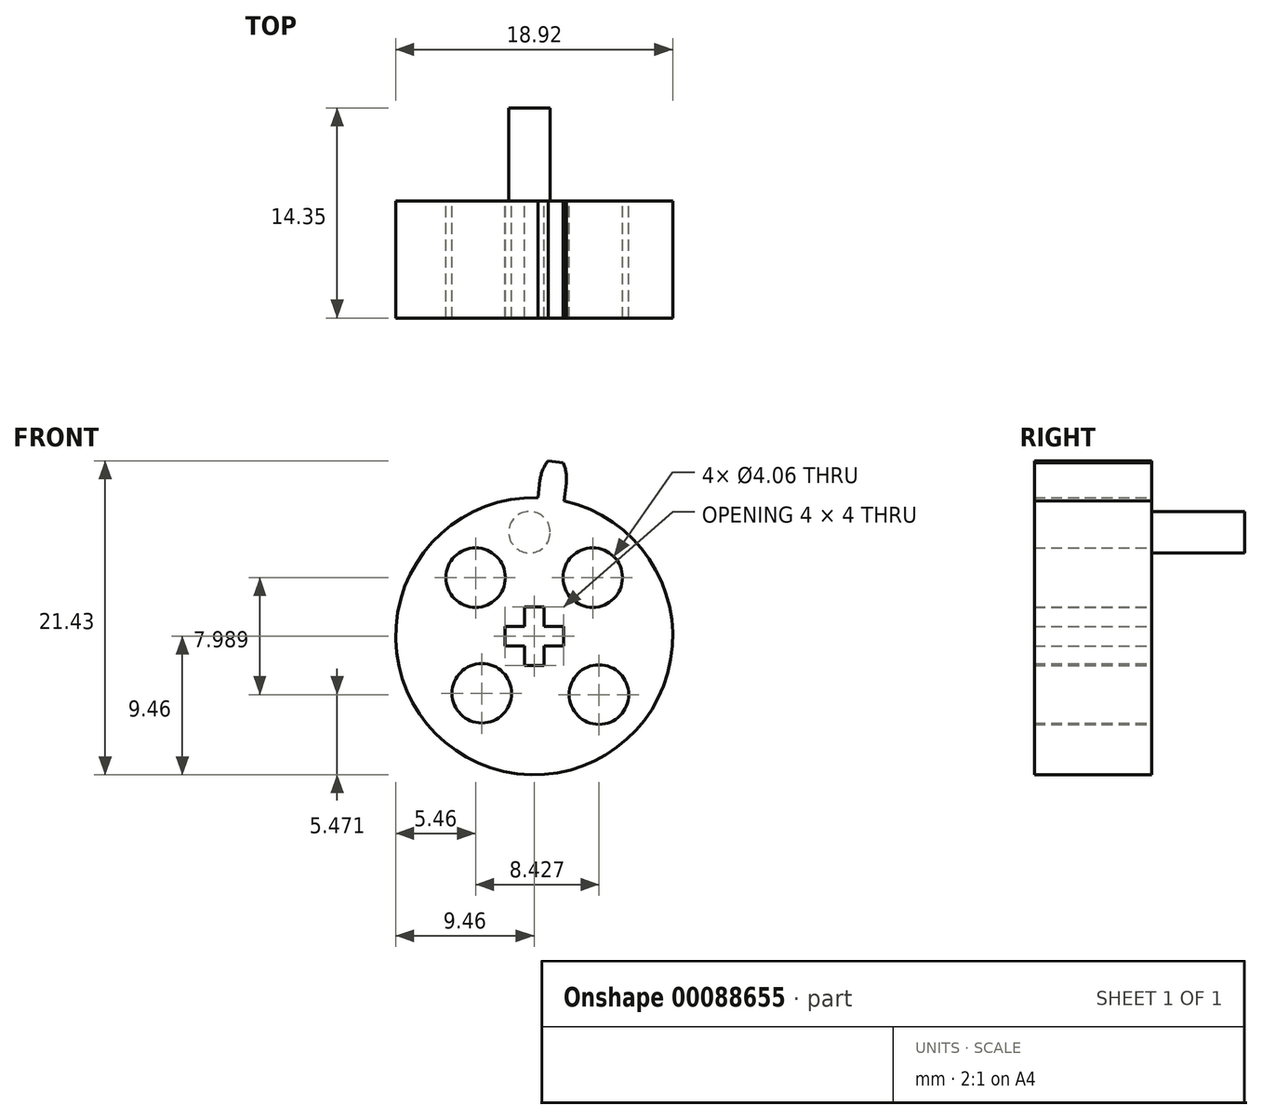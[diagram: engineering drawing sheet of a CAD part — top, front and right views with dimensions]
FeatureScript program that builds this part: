
annotation { "Feature Type Name" : "Feature", "Feature Type Description" : "" }
export const myFeature = defineFeature(function(context is Context, id is Id, definition is map)
    precondition{}
    {
        {
            var Q0;
            Q0=qCreatedBy(makeId("Front.planeOp"),FACE);
            var sketch = newSketch(context, id + "F0", { "sketchPlane" : qUnion([Q0])});
            skLineSegment(sketch, "E0", {"start": v(0.96, 11.97) * mm, "end": v(1.97, 11.85) * mm});
            skArc(sketch, "E1", {"start": v(0.25, 9.46) * mm, "mid": v(1.15, 9.39) * mm, "end": v(2.05, 9.24) * mm});
            skLineSegment(sketch, "E2", {"start": v(0.4, 10.67) * mm, "end": v(0.25, 9.46) * mm});
            skLineSegment(sketch, "E3.MirrorCS", {"start": v(2.2, 10.45) * mm, "end": v(2.05, 9.24) * mm});
            skLineSegment(sketch, "E4", {"start": v(1.15, 9.39) * mm, "end": v(1.5, 12.2) * mm, "construction": true});
            skArc(sketch, "E5", {"start": v(0.96, 11.97) * mm, "mid": v(0.59, 11.36) * mm, "end": v(0.4, 10.67) * mm});
            skArc(sketch, "E6", {"start": v(2.2, 10.45) * mm, "mid": v(2.18, 11.16) * mm, "end": v(1.97, 11.85) * mm});
            skSolve(sketch);
        }
        {
            var Q0;
            Q0=qCreatedBy(makeId("Top.planeOp"),FACE);
            var sketch = newSketch(context, id + "F1", { "sketchPlane" : qUnion([Q0])});
            skLineSegment(sketch, "E7", {"start": v(0, 0) * mm, "end": v(0, 30.53) * mm, "construction": true});
            skLineSegment(sketch, "E8", {"start": v(0, 0) * mm, "end": v(0, -25.91) * mm, "construction": true});
            skSolve(sketch);
        }
        {
            var Q0;
            Q0=qCreatedBy(makeId("Front.planeOp"),FACE);
            var sketch = newSketch(context, id + "F2", { "sketchPlane" : qUnion([Q0])});
            skCircle(sketch, "E9", {"center": v(0, 0) * mm, "radius": 9.46 * mm});
            skCircle(sketch, "E10", {"center": v(-4, 4) * mm, "radius": 2.03 * mm});
            skCircle(sketch, "E11.1.0.0", {"center": v(4, 4) * mm, "radius": 2.03 * mm});
            skLineSegment(sketch, "E11.direction1", {"start": v(-4, 4) * mm, "end": v(4, 4) * mm, "construction": true});
            skCircle(sketch, "E12.0.1.0", {"center": v(4.43, -3.99) * mm, "radius": 2.03 * mm});
            skLineSegment(sketch, "E12.direction1", {"start": v(4, 4) * mm, "end": v(23.14, 4) * mm, "construction": true});
            skLineSegment(sketch, "E12.direction2", {"start": v(4, 4) * mm, "end": v(4.43, -3.99) * mm, "construction": true});
            skCircle(sketch, "E13.1.0.0", {"center": v(-3.57, -3.9) * mm, "radius": 2.03 * mm});
            skLineSegment(sketch, "E13.direction1", {"start": v(4.43, -3.99) * mm, "end": v(-3.57, -3.9) * mm, "construction": true});
            skSolve(sketch);
        }
        {
            var Q0;
            Q0=makeQuery(id+"F2.imprint","IMPRINT",FACE,{"disambiguationData":[TD([[makeQuery(id+"F2.imprint","IMPRINT",EDGE,{"derivedFrom":sQuery(id+"F2.wireOp",EDGE,"E9")}),1.0]])]});
            extrude(context, id + "F3", {"entities" : qUnion([Q0]), "depth" : 8 * mm});
        }
        {
            var Q0;
            Q0=makeQuery(id+"F0.imprint","IMPRINT",FACE,{"disambiguationData":[TD([[makeQuery(id+"F0.imprint","IMPRINT",EDGE,{"derivedFrom":sQuery(id+"F0.wireOp",EDGE,"E0")}),-1.0]])]});
            var Q1;
            Q1=makeQuery(id+"F3.opExtrude","CAP_FACE",FACE,{"disambiguationData":[OSD([sQuery(id+"F2.wireOp",EDGE,"E9"),sQuery(id+"F2.wireOp",EDGE,"E10"),sQuery(id+"F2.wireOp",EDGE,"E11.1.0.0"),sQuery(id+"F2.wireOp",EDGE,"E12.0.1.0"),sQuery(id+"F2.wireOp",EDGE,"E13.1.0.0")])],"isStart":false});
            extrude(context, id + "F4", {"entities" : qUnion([Q0]), "operationType" : NewBodyOperationType.ADD, "endBound" : BoundingType.UP_TO_SURFACE, "endBoundEntityFace" : qUnion([Q1]), "depth" : 25.4 * mm});
        }
        {
            var Q0;
            Q0=qCreatedBy(makeId("Front.planeOp"),FACE);
            var sketch = newSketch(context, id + "F5", { "sketchPlane" : qUnion([Q0])});
            skLineSegment(sketch, "E14", {"start": v(0, 3.5) * mm, "end": v(0, -4.5) * mm, "construction": true});
            skLineSegment(sketch, "E15", {"start": v(0.67, 2) * mm, "end": v(0.67, 0.67) * mm});
            skLineSegment(sketch, "E16", {"start": v(0.67, 0.67) * mm, "end": v(2, 0.67) * mm});
            skLineSegment(sketch, "E17", {"start": v(2, 0.67) * mm, "end": v(2, 0) * mm});
            skLineSegment(sketch, "E18", {"start": v(0.67, 2) * mm, "end": v(0, 2) * mm});
            skLineSegment(sketch, "E19", {"start": v(3.85, 0) * mm, "end": v(-2.03, 0) * mm, "construction": true});
            skArc(sketch, "E20.0", {"start": v(0.25, 9.46) * mm, "mid": v(-0.08, 9.46) * mm, "end": v(-0.41, 9.45) * mm});
            skArc(sketch, "E21.0", {"start": v(9.46, -0.25) * mm, "mid": v(9.46, 0.08) * mm, "end": v(9.45, 0.41) * mm, "construction": true});
            skLineSegment(sketch, "E22", {"start": v(-0.08, 9.46) * mm, "end": v(-0.08, 7.09) * mm, "construction": true});
            skLineSegment(sketch, "E23", {"start": v(9.46, 0.08) * mm, "end": v(6.56, 0.08) * mm, "construction": true});
            skLineSegment(sketch, "E24.MirrorCS", {"start": v(2, -0.67) * mm, "end": v(2, 0) * mm});
            skLineSegment(sketch, "E25.MirrorCS", {"start": v(0.67, -0.67) * mm, "end": v(2, -0.67) * mm});
            skLineSegment(sketch, "E26.MirrorCS", {"start": v(0.67, -2) * mm, "end": v(0.67, -0.67) * mm});
            skLineSegment(sketch, "E27.MirrorCS", {"start": v(0.67, -2) * mm, "end": v(0, -2) * mm});
            skLineSegment(sketch, "E28.MirrorCS", {"start": v(-0.67, 2) * mm, "end": v(0, 2) * mm});
            skLineSegment(sketch, "E29.MirrorCS", {"start": v(-0.67, 2) * mm, "end": v(-0.67, 0.67) * mm});
            skLineSegment(sketch, "E30.MirrorCS", {"start": v(-0.67, 0.67) * mm, "end": v(-2, 0.67) * mm});
            skLineSegment(sketch, "E31.MirrorCS", {"start": v(-2, 0.67) * mm, "end": v(-2, 0) * mm});
            skLineSegment(sketch, "E32.MirrorCS", {"start": v(-2, -0.67) * mm, "end": v(-2, 0) * mm});
            skLineSegment(sketch, "E33.MirrorCS", {"start": v(-0.67, -0.67) * mm, "end": v(-2, -0.67) * mm});
            skLineSegment(sketch, "E34.MirrorCS", {"start": v(-0.67, -2) * mm, "end": v(-0.67, -0.67) * mm});
            skLineSegment(sketch, "E35.MirrorCS", {"start": v(-0.67, -2) * mm, "end": v(0, -2) * mm});
            skSolve(sketch);
        }
        {
            var Q0;
            Q0 = qSketchRegion(id + "F5", true);
            extrude(context, id + "F6", {"entities" : qUnion([Q0]), "operationType" : NewBodyOperationType.REMOVE, "depth" : 25.4 * mm});
        }
        {
            var Q0;
            Q0=qCreatedBy(makeId("Front.planeOp"),FACE);
            var sketch = newSketch(context, id + "F7", { "sketchPlane" : qUnion([Q0])});
            skCircle(sketch, "E36", {"center": v(-0.32, 7.1) * mm, "radius": 1.42 * mm});
            skSolve(sketch);
        }
        {
            var Q0;
            Q0 = qSketchRegion(id + "F7", true);
            extrude(context, id + "F8", {"entities" : qUnion([Q0]), "operationType" : NewBodyOperationType.ADD, "oppositeDirection" : true, "depth" : 6.35 * mm});
        }
    });
